# Revit family: EKF_EE_ПультУправленияНапольный_IP55_PROxima
name_source: partatom
category: Электрооборудование
units: mm (PartAtom-declared; Revit-internal decimal feet)

## family parameters
Всегда вертикально = Да
На основе рабочей плоскости = Нет
Общий = Нет
При загрузке вырезать с полостями = Нет
Размер круглого соединителя = Использовать диаметр
Тип детали = Силовой щит
Точка расчета площади = Да

## types (5) — shared parameters
ADSK_Единица измерения = компл.
ADSK_Завод-изготовитель = EKF
ADSK_Классификация нагрузок = Прочее
ADSK_Количество = 1
ADSK_Количество фаз = 3
ADSK_Коэффициент мощности = 1
ADSK_Марка = Пульт управления
ADSK_Материал = RAL 7035_Сталь
ADSK_Напряжение = 400 В
ADSK_Номинальная мощность = 0 Вт
ADSK_Обозначение = Пульт управления
ADSK_Полная мощность = 0 В·А
ADSK_Размер_Высота = 960 мм
ADSK_Размер_Глубина = 400 мм
ADSK_Ток = 0 А
Изготовитель = EKF
Комплект = -
Серия номенклатуры = PROxima
Степень защиты IP = IP55
ТВ = EKF_2
Тип установки = Напольный
zero-valued in all types: ADSK_Масса, Количество DIN-реек, Количество модулей на DIN-рейке, Максимальное количество модулей

## per-type parameters (varying)
| type | ADSK_Код изделия | ADSK_Размер_Ширина | Тип |
| Пульт управления напольный 2-ст. обсл. TP6 IP55 (960х600х400) EKF PROxima | mb-96-60-40m | 600 мм | 160 мм |
| Пульт управления напольный TP10 IP55 (960х1000х400) | mb-96-100-40 | 1000 мм | 161 мм |
| Пульт управления напольный TP12 IP55 (960х1200х400) | mb-96-120-40 | 1200 мм | 162 мм |
| Пульт управления напольный TP6 IP55 (960х600х400) | mb-96-60-40 | 600 мм | 163 мм |
| Пульт управления напольный TP8 IP55 (960х800х400) | mb-96-80-40 | 800 мм | 164 мм |

note: column(s) folded — value = type name in every type: ADSK_Наименование
